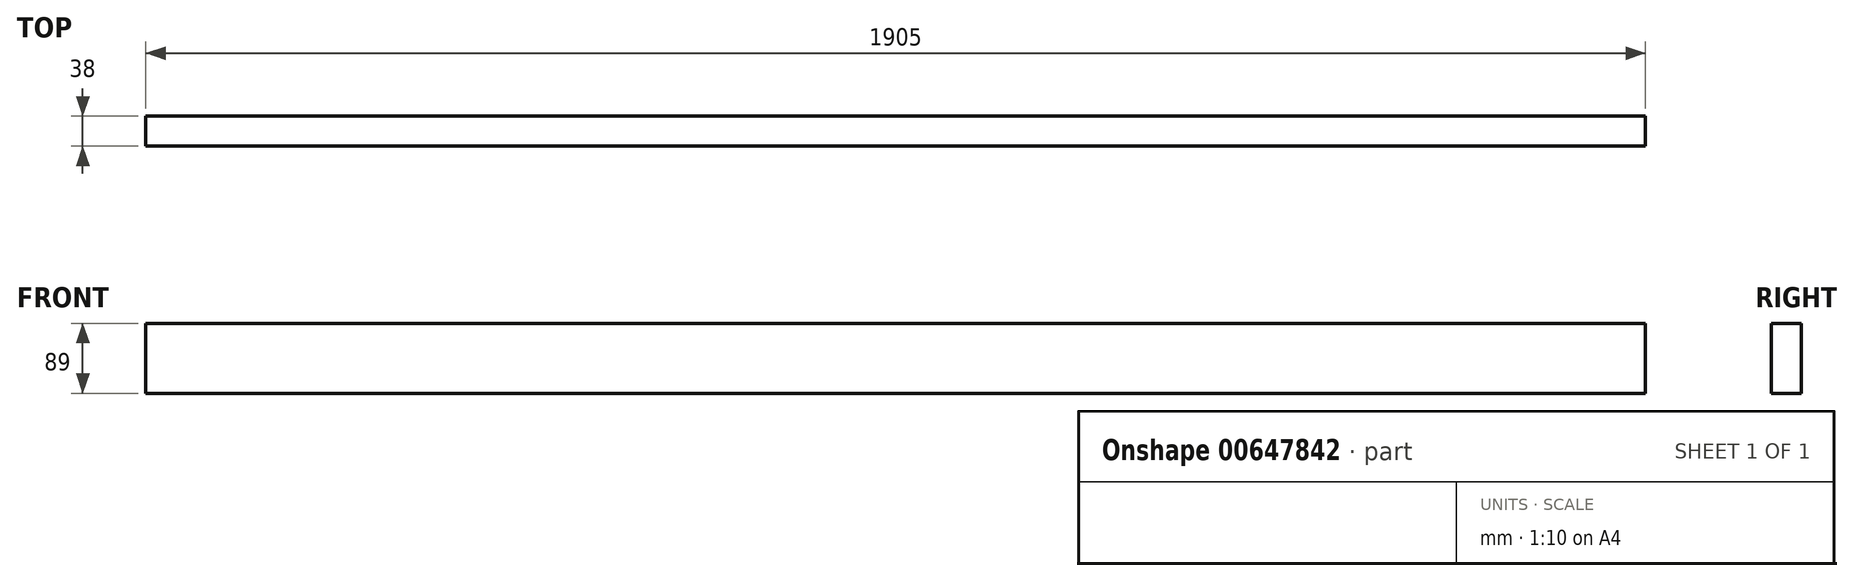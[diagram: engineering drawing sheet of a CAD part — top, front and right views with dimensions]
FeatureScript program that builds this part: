
annotation { "Feature Type Name" : "Feature", "Feature Type Description" : "" }
export const myFeature = defineFeature(function(context is Context, id is Id, definition is map)
    precondition{}
    {
        {
            var Q0;
            Q0=qCreatedBy(makeId("Front.planeOp"),FACE);
            var sketch = newSketch(context, id + "F0", { "sketchPlane" : qUnion([Q0])});
            skLineSegment(sketch, "E0.bottom", {"start": v(-952.5, 44.5) * mm, "end": v(952.5, 44.5) * mm});
            skLineSegment(sketch, "E0.top", {"start": v(-952.5, -44.5) * mm, "end": v(952.5, -44.5) * mm});
            skLineSegment(sketch, "E0.left", {"start": v(-952.5, 44.5) * mm, "end": v(-952.5, -44.5) * mm});
            skLineSegment(sketch, "E0.right", {"start": v(952.5, 44.5) * mm, "end": v(952.5, -44.5) * mm});
            skPoint(sketch, "E0.middle", {"position": v(0, 0) * mm});
            skSolve(sketch);
        }
        {
            var Q0;
            Q0 = qSketchRegion(id + "F0", true);
            extrude(context, id + "F1", {"entities" : qUnion([Q0]), "depth" : 38 * mm, "offsetDistance" : 25 * mm});
        }
    });
